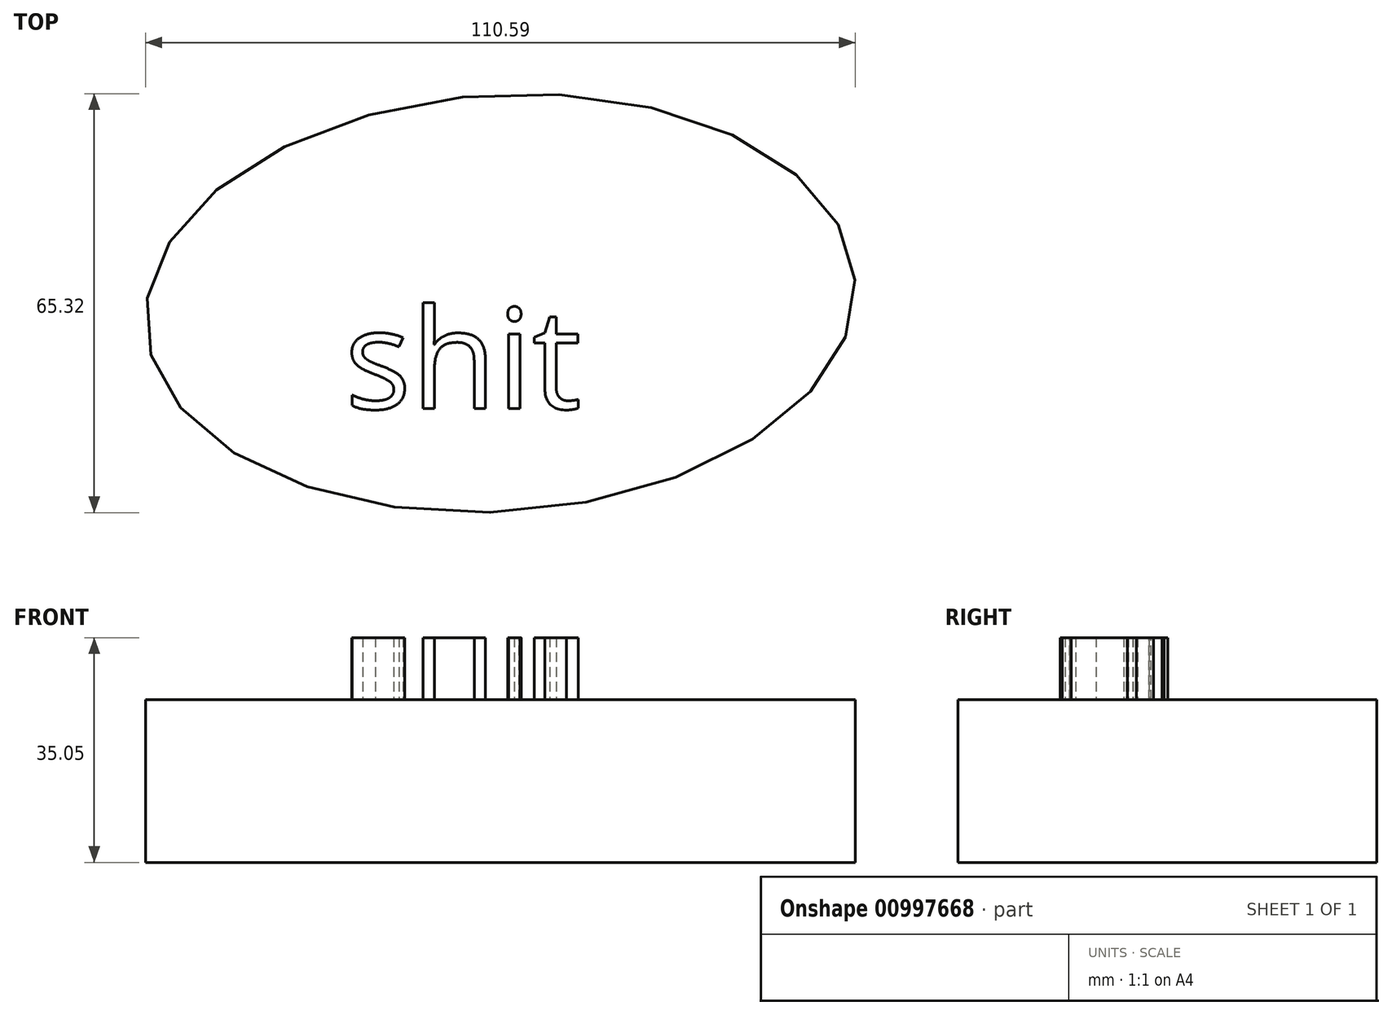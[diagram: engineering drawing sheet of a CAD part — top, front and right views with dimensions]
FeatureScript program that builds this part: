
annotation { "Feature Type Name" : "Feature", "Feature Type Description" : "" }
export const myFeature = defineFeature(function(context is Context, id is Id, definition is map)
    precondition{}
    {
        {
            var Q0;
            Q0=qCreatedBy(makeId("Top.planeOp"),FACE);
            var sketch = newSketch(context, id + "F0", { "sketchPlane" : qUnion([Q0])});
            skEllipse(sketch, "E0", {"center": v(-17.86, -7.63) * mm, "majorRadius": 55.37 * mm, "minorRadius": 32.53 * mm, "majorAxis": v(1, 0.07)});
            skSolve(sketch);
        }
        {
            var Q0;
            Q0 = qSketchRegion(id + "F0", true);
            extrude(context, id + "F1", {"entities" : qUnion([Q0]), "depth" : 25.4 * mm, "offsetDistance" : 25.4 * mm});
        }
        {
            var Q0;
            Q0=makeQuery(id+"F1.opExtrude","CAP_FACE",FACE,{"disambiguationData":[OSD([sQuery(id+"F0.wireOp",EDGE,"E0")])],"isStart":false});
            var sketch = newSketch(context, id + "F2", { "sketchPlane" : qUnion([Q0])});
            skText(sketch, "E1", { "text": "shit\n\n", "fontName": "OpenSans-Regular.ttf"});
            const initialGuessF2  = {"E1": [-0.04214, -0.02409, 1, 0, 0.01565]};
            skSetInitialGuess(sketch, initialGuessF2);
            skSolve(sketch);
        }
        {
            var Q0;
            Q0 = qSketchRegion(id + "F2", true);
            extrude(context, id + "F3", {"entities" : qUnion([Q0]), "operationType" : NewBodyOperationType.ADD, "depth" : 9.65 * mm, "offsetDistance" : 25.4 * mm});
        }
    });
